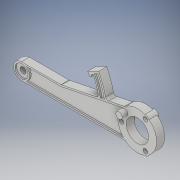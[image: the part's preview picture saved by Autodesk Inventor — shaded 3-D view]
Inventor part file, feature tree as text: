
AUTODESK INVENTOR PART (.ipt)
format: ipt  version: 2019 (Build 230136000, 136)  size: 262,656 bytes
history: native  units: in
note: dims shown in document units (in); Inventor stores cm internally (conversion verified against a paired STEP export)
features: sketch x9, extrude x8, fillet x2, hole x1, pattern_circular x1
ambient origin geometry x8: Origin, YZ Plane, XZ Plane, XY Plane, X Axis, Y Axis, Z Axis, Center Point
bodies: Solid1 (feature_tree)
feature tree (21):
  extrude  "Extrusion1"  Depth=0.8in
  extrude  "Extrusion2"  Depth=1.44in
  hole  "Hole1"  [1 undecoded]
  pattern_circular  "Circular Pattern1"  Count=3 Angle=360.0deg
  extrude  "Extrusion4"  Depth=0.08in TaperAngle=0.0deg
  extrude  "Extrusion3"  Depth=0.36in
  fillet  "Fillet1"  Radius=0.36in
  extrude  "Extrusion5"  Depth=0.2in
  extrude  "Extrusion6"  Depth=0.115in
  extrude  "Extrusion7"  Depth=0.125in
  extrude  "Extrusion9"  Depth=0.786in
  fillet  "Fillet3"  Radius=0.08in
  sketch  "Sketch1"  dims[d0=1.888in d1=0.8in]
  sketch  "Sketch2"  dims[d4=5.5in d5=1.44in]
  sketch  "Sketch3"  dims[d6=0.395in d7=0.0in d8=0.3in]
  sketch  "Sketch4"  dims[d9=1.1in]
  sketch  "Sketch5"  dims[d10=0.395in d11=0.0in]
  sketch  "Sketch6"  dims[d14=0.125in d15=0.75in d16=0.225in d17=0.125in d18=0.5635in d19=1.0in d20=0.8108in d21=1.1811in d22=360.0deg]
  sketch  "Sketch7"  dims[d24=0.08in d25=0.08in d26=0.0in]
  sketch  "Sketch8"  dims[d27=0.08in d29=8.5in d30=0.36in]
  sketch  "Sketch10"  dims[d32=15.0deg d33=0.2in d34=0.115in d35=0.125in d36=0.6in d37=0.08in d38=0.0in d39=0.08in d40=0.125in d41=0.385in d42=1.1811in d44=360.0deg d46=0.47in d47=0.0in d48=0.315in d49=0.28in d50=0.0in d51=0.38in d52=0.0in d58=0.16in d59=0.25in d60=0.0in d61=0.786in]
note: 1 required parameter value undecoded (feature->parameter linkage not recoverable at this tier; creation-order binding heuristic only, values carry confidence <= 0.55)
